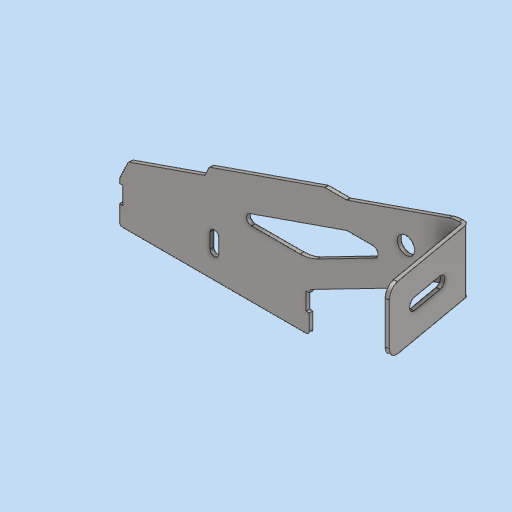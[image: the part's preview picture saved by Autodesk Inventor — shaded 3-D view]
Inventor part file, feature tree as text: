
AUTODESK INVENTOR PART (.ipt)
format: ipt  version: 2023 (Build 270158000, 158)  size: 219,136 bytes
history: native  units: in
note: dims shown in document units (in); Inventor stores cm internally (conversion verified against a paired STEP export)
features: other x4, sketch x1, plane x1
ambient origin geometry x8: Origin, YZ Plane, XZ Plane, XY Plane, X Axis, Y Axis, Z Axis, Center Point
bodies: Body1 (feature_tree)
feature tree (6):
  other  "吊架-短(R) - 焊接件-1(v220714).ipt"
  other  "實體1::吊架-短(R) - 焊接件-1(v220714).ipt"
  other  "標籤特徵1"
  sketch  "草圖1"
  plane  "工作平面1"
  other  "實體1"
